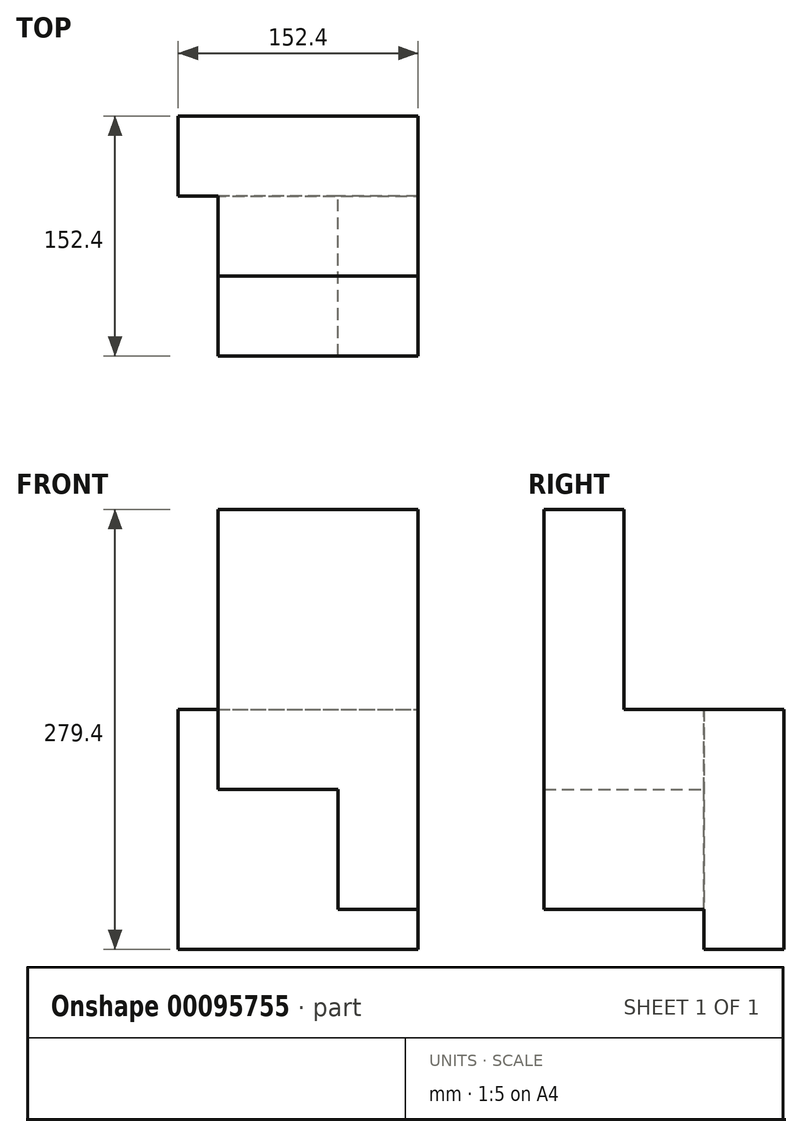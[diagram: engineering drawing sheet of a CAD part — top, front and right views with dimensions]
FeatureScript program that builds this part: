
annotation { "Feature Type Name" : "Feature", "Feature Type Description" : "" }
export const myFeature = defineFeature(function(context is Context, id is Id, definition is map)
    precondition{}
    {
        {
            var Q0;
            Q0=qCreatedBy(makeId("Front.planeOp"),FACE);
            var sketch = newSketch(context, id + "F0", { "sketchPlane" : qUnion([Q0])});
            skLineSegment(sketch, "E0.bottom", {"start": v(-82.8, 87.13) * mm, "end": v(69.6, 87.13) * mm});
            skLineSegment(sketch, "E0.top", {"start": v(-82.8, -39.87) * mm, "end": v(69.6, -39.87) * mm});
            skLineSegment(sketch, "E0.left", {"start": v(-82.8, 87.13) * mm, "end": v(-82.8, -39.87) * mm});
            skLineSegment(sketch, "E0.right", {"start": v(69.6, 87.13) * mm, "end": v(69.6, -39.87) * mm});
            skSolve(sketch);
        }
        {
            var Q0;
            Q0 = qSketchRegion(id + "F0", true);
            extrude(context, id + "F1", {"entities" : qUnion([Q0]), "depth" : 50.8 * mm});
        }
        {
            var Q0;
            Q0=makeQuery(id+"F1.opExtrude","CAP_FACE",FACE,{"disambiguationData":[OSD([sQuery(id+"F0.wireOp",EDGE,"E0.bottom"),sQuery(id+"F0.wireOp",EDGE,"E0.top"),sQuery(id+"F0.wireOp",EDGE,"E0.left"),sQuery(id+"F0.wireOp",EDGE,"E0.right")])],"isStart":false});
            var sketch = newSketch(context, id + "F2", { "sketchPlane" : qUnion([Q0])});
            skLineSegment(sketch, "E1", {"start": v(69.6, -14.47) * mm, "end": v(18.8, -14.47) * mm});
            skLineSegment(sketch, "E2", {"start": v(18.8, -14.47) * mm, "end": v(18.8, 61.73) * mm});
            skLineSegment(sketch, "E3", {"start": v(18.8, 61.73) * mm, "end": v(-57.4, 61.73) * mm});
            skLineSegment(sketch, "E4", {"start": v(-57.4, 61.73) * mm, "end": v(-57.4, 87.13) * mm});
            skLineSegment(sketch, "E5", {"start": v(-57.4, 87.13) * mm, "end": v(69.6, 87.13) * mm});
            skLineSegment(sketch, "E6", {"start": v(69.6, 87.13) * mm, "end": v(69.6, -14.47) * mm});
            skSolve(sketch);
        }
        {
            var Q0;
            Q0 = qSketchRegion(id + "F2", true);
            extrude(context, id + "F3", {"entities" : qUnion([Q0]), "operationType" : NewBodyOperationType.ADD, "depth" : 101.6 * mm});
        }
        {
            var Q0;
            Q0=makeQuery(id+"F3.boolean.opBoolean","MERGE",FACE,{"derivedFrom":[makeQuery(id+"F1.opExtrude","SWEPT_FACE",FACE,{"disambiguationData":[OSD([sQuery(id+"F0.wireOp",EDGE,"E0.bottom")])]}),makeQuery(id+"F3.opExtrude","SWEPT_FACE",FACE,{"disambiguationData":[OSD([sQuery(id+"F2.wireOp",EDGE,"E5")])]})]});
            var sketch = newSketch(context, id + "F4", { "sketchPlane" : qUnion([Q0])});
            skLineSegment(sketch, "E7", {"start": v(-82.8, 0) * mm, "end": v(-82.8, -50.8) * mm});
            skLineSegment(sketch, "E8", {"start": v(-82.8, -50.8) * mm, "end": v(-57.4, -50.8) * mm});
            skLineSegment(sketch, "E9", {"start": v(-57.4, -50.8) * mm, "end": v(-57.4, -152.4) * mm});
            skLineSegment(sketch, "E10", {"start": v(-57.4, -152.4) * mm, "end": v(69.6, -152.4) * mm});
            skLineSegment(sketch, "E11", {"start": v(69.6, -152.4) * mm, "end": v(69.6, 0) * mm});
            skLineSegment(sketch, "E12", {"start": v(69.6, 0) * mm, "end": v(-82.8, 0) * mm});
            skSolve(sketch);
        }
        {
            var Q0;
            Q0 = qSketchRegion(id + "F4", true);
            extrude(context, id + "F5", {"entities" : qUnion([Q0]), "operationType" : NewBodyOperationType.ADD, "depth" : 25.4 * mm});
        }
        {
            var Q0;
            Q0=makeQuery(id+"F5.opExtrude","CAP_FACE",FACE,{"disambiguationData":[OSD([sQuery(id+"F4.wireOp",EDGE,"E7"),sQuery(id+"F4.wireOp",EDGE,"E8"),sQuery(id+"F4.wireOp",EDGE,"E9"),sQuery(id+"F4.wireOp",EDGE,"E10"),sQuery(id+"F4.wireOp",EDGE,"E11"),sQuery(id+"F4.wireOp",EDGE,"E12")])],"isStart":false});
            var sketch = newSketch(context, id + "F6", { "sketchPlane" : qUnion([Q0])});
            skLineSegment(sketch, "E13.bottom", {"start": v(-57.4, -152.4) * mm, "end": v(69.6, -152.4) * mm});
            skLineSegment(sketch, "E13.top", {"start": v(-57.4, -101.6) * mm, "end": v(69.6, -101.6) * mm});
            skLineSegment(sketch, "E13.left", {"start": v(-57.4, -152.4) * mm, "end": v(-57.4, -101.6) * mm});
            skLineSegment(sketch, "E13.right", {"start": v(69.6, -152.4) * mm, "end": v(69.6, -101.6) * mm});
            skSolve(sketch);
        }
        {
            var Q0;
            Q0 = qSketchRegion(id + "F6", true);
            extrude(context, id + "F7", {"entities" : qUnion([Q0]), "operationType" : NewBodyOperationType.ADD, "depth" : 127 * mm});
        }
    });
